# Revit family: Hager-Orion_Plus-IP65-D300-Cl.II-Poly_floor_encl-630A-NoHosted-CH-fr
name_source: partatom
category: Electrical Equipment
units: mm (PartAtom-declared; Revit-internal decimal feet)

## family parameters
Always vertical = Yes
Cut with Voids When Loaded = No
Panel Configuration = Two Columns, Circuits Across
Part Type = Panelboard
Room Calculation Point = No
Round Connector Dimension = Use Diameter
Shared = No
Work Plane-Based = Yes

## types (18) — shared parameters
Default Elevation = 1219 mm
EF000003 - mode de pose = EV012274 - installation au sol
EF000007 - couleur = EV000270 - gris
EF000049 - profondeur = 300 mm  [stored 0.984252 ft]
EF000116 - numéro RAL = 7035
EF000118 - avec cadre/support de montage = No
EF001596 - matériau du boîtier/corps = EV000139 - plastique
EF001613 - maintien de fonction = EV000494 - sans
EF003532 - convient pour utilisation à l’extérieur = Yes
EF004464 - type de porte = EV002646 - unique
EF005474 - indice de protection (IP) = EV006421 - IP65
EF006306 - avec serrure = Yes
EF007800 - adapté à un parafoudre = No
EF008873 - courant nominal (In) = 630 A
EF009170 - épaisseur de matériau du boîtier = 2 mm  [stored 0.00656168 ft]
EF009171 - épaisseur de matériau de la porte/du couvercle = 2 mm  [stored 0.00656168 ft]
EF015940 - couvercle avec décharge de pression = No
HG000002 - avec porte = Yes
HG000003 - Gamme = Orion Plus
HG000006 - Encastré = No
HG000009 - Porte à double battant = No
HG000010 - Portes asymétriques = No
HG000023 - Armoire double section = No
HG000024 - Hauteur de la section basse = 600 mm
HG000026 - Installation au sol = Yes
HG000027 - Hauteur du socle = 70 mm  [stored 0.229659 ft]
Manufacturer = Hager
Type Comments = Orion Plus
zero-valued in all types: EF000218 - profondeur d'encastrement, EF002950 - largeur en nombre de modules

## per-type parameters (varying)
| type | EF000008 - largeur | EF000040 - hauteur | EF000266 - nombre de rangées | EF000339 - type de capot | EF000437 - nombre d'entrées de conduit | EF001088 - possibilité de montage en saillie | EF001131 - profondeur intérieure | EF004293 - indice de protection contre les chocs (IK) | EF004427 - nombre de modules | EF006244 - couvercle/porte transparent(e) | EF009212 - finition du couvercle | EF009554 - nombre d'ouvertures pour plaques à bride | HG000004 - Référence fabricant |
| installation au sol IP65 L1100 H1200 P300  - FL332B | 1100 mm | 1200 mm | 7 | EV004216 - porte | 0 | Yes | 300 mm  [stored 0.984252 ft] | EV008784 - IK10 | 322 | Yes | EV009916 - avec échancrure | 0 | FL332B |
| installation au sol IP65 L1100 H1200 P300  - FL532B | 1100 mm | 1200 mm | 7 | EV004216 - porte | 0 | Yes | 300 mm  [stored 0.984252 ft] | EV008784 - IK10 | 322 | Yes | EV000116 - fermé | 0 | FL532B |
| installation au sol IP65 L1100 H600 P300  - FL330B | 1100 mm | 600 mm | 3 | EV004216 - porte | 0 | Yes | 300 mm  [stored 0.984252 ft] | EV008784 - IK10 | 138 | Yes | EV009916 - avec échancrure | 0 | FL330B |
| installation au sol IP65 L1100 H600 P300  - FL530B | 1100 mm | 600 mm | 3 | EV004216 - porte | 0 | Yes | 300 mm  [stored 0.984252 ft] | EV008784 - IK10 | 138 | Yes | EV000116 - fermé | 0 | FL530B |
| installation au sol IP65 L1100 H900 P300  - FL331B | 1100 mm | 900 mm  [stored 2.95276 ft] | 5 | EV004216 - porte | 0 | Yes | 300 mm  [stored 0.984252 ft] | EV008784 - IK10 | 230 | Yes | EV009916 - avec échancrure | 0 | FL331B |
| installation au sol IP65 L1100 H900 P300  - FL531B | 1100 mm | 900 mm  [stored 2.95276 ft] | 5 | EV004216 - porte | 0 | Yes | 300 mm  [stored 0.984252 ft] | EV008784 - IK10 | 230 | Yes | EV000116 - fermé | 0 | FL531B |
| installation au sol IP65 L600 H1200 P300  - FL322B | 600 mm | 1200 mm | 7 | EV004216 - porte | 0 | Yes | 300 mm  [stored 0.984252 ft] | EV008784 - IK10 | 161 | Yes | EV009916 - avec échancrure | 0 | FL322B |
| installation au sol IP65 L600 H1200 P300  - FL522B | 600 mm | 1200 mm | 7 | EV004216 - porte | 0 | Yes | 300 mm  [stored 0.984252 ft] | EV008784 - IK10 | 161 | Yes | EV000116 - fermé | 0 | FL522B |
| installation au sol IP65 L600 H600 P300  - FL320B | 600 mm | 600 mm | 3 | EV004216 - porte | 0 | Yes | 200 mm  [stored 0.656168 ft] | EV008784 - IK10 | 69 | Yes | EV009916 - avec échancrure | 0 | FL320B |
| installation au sol IP65 L600 H600 P300  - FL520B | 600 mm | 600 mm | 3 | EV004216 - porte | 0 | Yes | 300 mm  [stored 0.984252 ft] | EV008784 - IK10 | 69 | Yes | EV000116 - fermé | 0 | FL520B |
| installation au sol IP65 L600 H900 P300  - FL321B | 600 mm | 900 mm  [stored 2.95276 ft] | 5 | EV004216 - porte | 0 | Yes | 300 mm  [stored 0.984252 ft] | EV008784 - IK10 | 115 | Yes | EV009916 - avec échancrure | 0 | FL321B |
| installation au sol IP65 L600 H900 P300  - FL521B | 600 mm | 900 mm  [stored 2.95276 ft] | 5 | EV004216 - porte | 0 | Yes | 300 mm  [stored 0.984252 ft] | EV008784 - IK10 | 115 | Yes | EV000116 - fermé | 0 | FL521B |
| installation au sol IP65 L850 H1200 P300  - FL327B | 850 mm  [stored 2.78871 ft] | 1200 mm | 7 | EV001012 - couvercle | 0 | No | 300 mm  [stored 0.984252 ft] | EV006814 - IK08 | 259 | No | EV000116 - fermé | 0 | FL327B |
| installation au sol IP65 L850 H1200 P300  - FL527B | 850 mm  [stored 2.78871 ft] | 1200 mm | 7 | EV004216 - porte | 0 | No | 235 mm  [stored 0.770997 ft] | EV008784 - IK10 | 259 | No | EV009916 - avec échancrure | 0 | FL527B |
| installation au sol IP65 L850 H600 P300  - FL325B | 850 mm  [stored 2.78871 ft] | 600 mm | 3 | EV004216 - porte | 2 | Yes | 300 mm  [stored 0.984252 ft] | EV008784 - IK10 | 111 | Yes | EV009916 - avec échancrure | 2 | FL325B |
| installation au sol IP65 L850 H600 P300  - FL525B | 850 mm  [stored 2.78871 ft] | 600 mm | 3 | EV004216 - porte | 0 | Yes | 300 mm  [stored 0.984252 ft] | EV008784 - IK10 | 111 | Yes | EV000116 - fermé | 0 | FL525B |
| installation au sol IP65 L850 H900 P300  - FL326B | 850 mm  [stored 2.78871 ft] | 900 mm  [stored 2.95276 ft] | 5 | EV004216 - porte | 0 | Yes | 300 mm  [stored 0.984252 ft] | EV008784 - IK10 | 185 | Yes | EV009916 - avec échancrure | 0 | FL326B |
| installation au sol IP65 L850 H900 P300  - FL526B | 850 mm  [stored 2.78871 ft] | 900 mm  [stored 2.95276 ft] | 5 | EV004216 - porte | 0 | Yes | 300 mm  [stored 0.984252 ft] | EV008784 - IK10 | 185 | Yes | EV000116 - fermé | 0 | FL526B |

note: [stored X ft] marks values corroborated as IEEE doubles in the binary element streams (Revit-internal decimal feet)

## geometry (parser evidence)
native form markers: Blend x4, Sweep x5
no freeform markers — native parametric forms only
